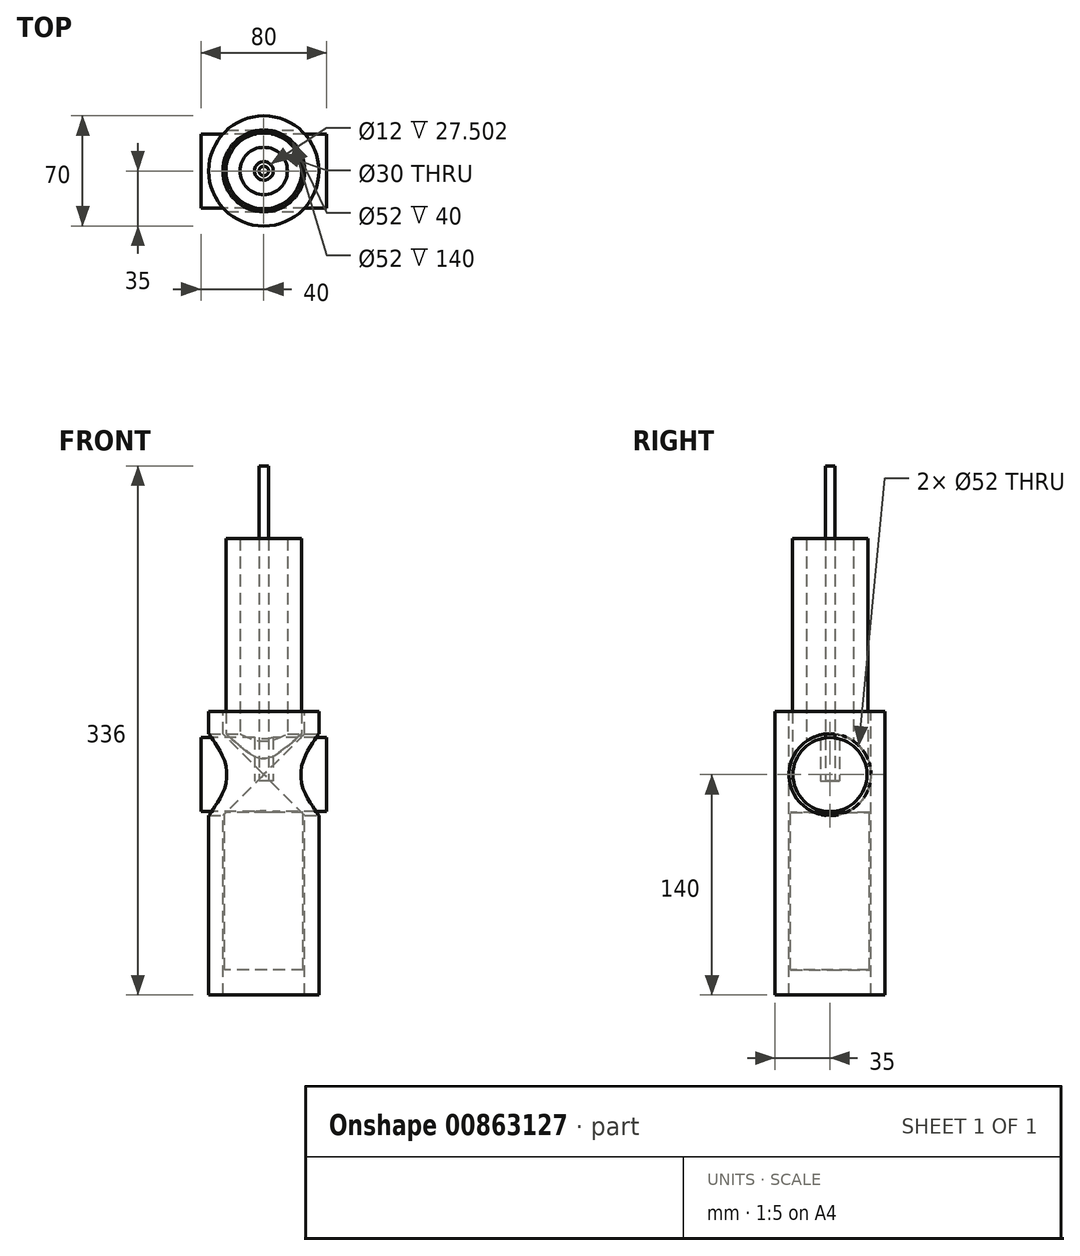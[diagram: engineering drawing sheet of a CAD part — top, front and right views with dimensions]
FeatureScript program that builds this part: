
annotation { "Feature Type Name" : "Feature", "Feature Type Description" : "" }
export const myFeature = defineFeature(function(context is Context, id is Id, definition is map)
    precondition{}
    {
        {
            var Q0;
            Q0=qCreatedBy(makeId("Top.planeOp"),FACE);
            var sketch = newSketch(context, id + "F0", { "sketchPlane" : qUnion([Q0])});
            skCircle(sketch, "E0", {"center": v(0, 0) * mm, "radius": 26 * mm});
            skCircle(sketch, "E1", {"center": v(0, 0) * mm, "radius": 35 * mm});
            skSolve(sketch);
        }
        {
            var Q0;
            Q0=qSketchRegion(id+"F0",true);
            extrude(context, id + "F1", {"entities" : qUnion([Q0]), "oppositeDirection" : true, "depth" : 180 * mm, "offsetDistance" : 25 * mm});
        }
        {
            var Q0;
            Q0=qCreatedBy(makeId("Top.planeOp"),FACE);
            cPlane(context, id + "F2", {"entities" : qUnion([Q0]), "cplaneType" : CPlaneType.OFFSET, "offset" : 40 * mm, "oppositeDirection" : true, "width" : 150 * mm, "height" : 150 * mm});
        }
        {
            var Q0;
            Q0=qCreatedBy(id+"F2.planeOp",FACE);
            var sketch = newSketch(context, id + "F3", { "sketchPlane" : qUnion([Q0])});
            skCircle(sketch, "E2", {"center": v(0, 0) * mm, "radius": 24 * mm});
            skCircle(sketch, "E3", {"center": v(0, 0) * mm, "radius": 15 * mm});
            skSolve(sketch);
        }
        {
            var Q0;
            Q0=qSketchRegion(id+"F3",true);
            extrude(context, id + "F4", {"entities" : qUnion([Q0]), "depth" : 150 * mm, "offsetDistance" : 25 * mm});
        }
        {
            var Q0;
            Q0=qCreatedBy(makeId("Right.planeOp"),FACE);
            var sketch = newSketch(context, id + "F5", { "sketchPlane" : qUnion([Q0])});
            skCircle(sketch, "E4", {"center": v(0, -40) * mm, "radius": 26 * mm});
            skSolve(sketch);
        }
        {
            var Q0;
            Q0=qSketchRegion(id+"F5",true);
            extrude(context, id + "F6", {"entities" : qUnion([Q0]), "operationType" : NewBodyOperationType.REMOVE, "endBound" : BoundingType.THROUGH_ALL, "oppositeDirection" : true, "depth" : 25 * mm, "offsetDistance" : 25 * mm, "hasSecondDirection" : true, "secondDirectionBound" : SecondDirectionBoundingType.THROUGH_ALL, "secondDirectionOppositeDirection" : false, "secondDirectionDepth" : 25 * mm});
        }
        {
            var Q0;
            Q0=qCreatedBy(makeId("Right.planeOp"),FACE);
            var sketch = newSketch(context, id + "F7", { "sketchPlane" : qUnion([Q0])});
            skCircle(sketch, "E5.0", {"center": v(0, -40) * mm, "radius": 26 * mm, "construction": true});
            skCircle(sketch, "E6", {"center": v(0, -40) * mm, "radius": 23.5 * mm});
            skSolve(sketch);
        }
        {
            var Q0;
            Q0=qSketchRegion(id+"F7",true);
            extrude(context, id + "F8", {"entities" : qUnion([Q0]), "depth" : 40 * mm, "offsetDistance" : 25 * mm, "hasSecondDirection" : true, "secondDirectionOppositeDirection" : true, "secondDirectionDepth" : 40 * mm});
        }
        {
            var Q0;
            Q0=qCreatedBy(makeId("Top.planeOp"),FACE);
            var sketch = newSketch(context, id + "F9", { "sketchPlane" : qUnion([Q0])});
            skCircle(sketch, "E7", {"center": v(0, 0) * mm, "radius": 6 * mm});
            skSolve(sketch);
        }
        {
            var Q0;
            Q0=qSketchRegion(id+"F9",true);
            extrude(context, id + "F10", {"entities" : qUnion([Q0]), "operationType" : NewBodyOperationType.REMOVE, "endBound" : BoundingType.THROUGH_ALL, "depth" : 25 * mm, "offsetDistance" : 25 * mm, "hasSecondDirection" : true, "secondDirectionBound" : SecondDirectionBoundingType.THROUGH_ALL, "secondDirectionOppositeDirection" : true, "secondDirectionDepth" : 25 * mm});
        }
        {
            var Q0;
            Q0=qCreatedBy(id+"F2.planeOp",FACE);
            cPlane(context, id + "F11", {"entities" : qUnion([Q0]), "cplaneType" : CPlaneType.OFFSET, "offset" : 24 * mm, "oppositeDirection" : true, "width" : 150 * mm, "height" : 150 * mm});
        }
        {
            var Q0;
            Q0=qCreatedBy(id+"F11.planeOp",FACE);
            var sketch = newSketch(context, id + "F12", { "sketchPlane" : qUnion([Q0])});
            skCircle(sketch, "E8", {"center": v(0, 0) * mm, "radius": 25 * mm});
            skSolve(sketch);
        }
        {
            var Q0;
            Q0 = qSketchRegion(id + "F12", true);
            extrude(context, id + "F13", {"entities" : qUnion([Q0]), "oppositeDirection" : true, "depth" : 100 * mm, "offsetDistance" : 25 * mm});
        }
        {
            var Q0;
            Q0=makeQuery(id+"F13.opExtrude","CAP_FACE",FACE,{"disambiguationData":[OSD([sQuery(id+"F12.wireOp",EDGE,"E8")])],"isStart":true});
            var sketch = newSketch(context, id + "F14", { "sketchPlane" : qUnion([Q0])});
            skCircle(sketch, "E9", {"center": v(0, 0) * mm, "radius": 6 * mm});
            skSolve(sketch);
        }
        {
            var Q0;
            Q0 = qSketchRegion(id + "F14", true);
            extrude(context, id + "F15", {"entities" : qUnion([Q0]), "operationType" : NewBodyOperationType.ADD, "depth" : 20 * mm, "offsetDistance" : 25 * mm});
        }
        {
            var Q0;
            Q0=makeQuery(id+"F15.opExtrude","CAP_FACE",FACE,{"disambiguationData":[OSD([sQuery(id+"F14.wireOp",EDGE,"E9")])],"isStart":false});
            var sketch = newSketch(context, id + "F16", { "sketchPlane" : qUnion([Q0])});
            skCircle(sketch, "E10", {"center": v(0, 0) * mm, "radius": 3 * mm});
            skSolve(sketch);
        }
        {
            var Q0;
            Q0 = qSketchRegion(id + "F16", true);
            extrude(context, id + "F17", {"entities" : qUnion([Q0]), "operationType" : NewBodyOperationType.ADD, "depth" : 200 * mm, "offsetDistance" : 25 * mm});
        }
    });
